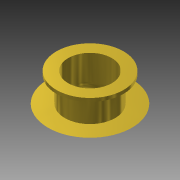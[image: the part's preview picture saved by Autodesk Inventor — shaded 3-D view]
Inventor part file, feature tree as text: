
AUTODESK INVENTOR PART (.ipt)
format: ipt  version: 2015 (Build 190159000, 159)  size: 143,360 bytes
history: native  units: mm
features: reference x3, sketch x2, other x1, revolve x1, hole x1, fillet x1
ambient origin geometry x8: Origin, YZ Plane, XZ Plane, XY Plane, X Axis, Y Axis, Z Axis, Center Point
bodies: Body1 (feature_tree)
feature tree (9):
  other  "솔리드1"
  revolve  "회전1"
  hole  "구멍1"  [1 undecoded]
  fillet  "모깎기1"  Radius=0.3mm
  sketch  "스케치1"
  reference  "참조1"
  reference  "참조2"
  reference  "참조3"
  sketch  "스케치2"
note: 1 required parameter value undecoded (feature->parameter linkage not recoverable at this tier; creation-order binding heuristic only, values carry confidence <= 0.55)
